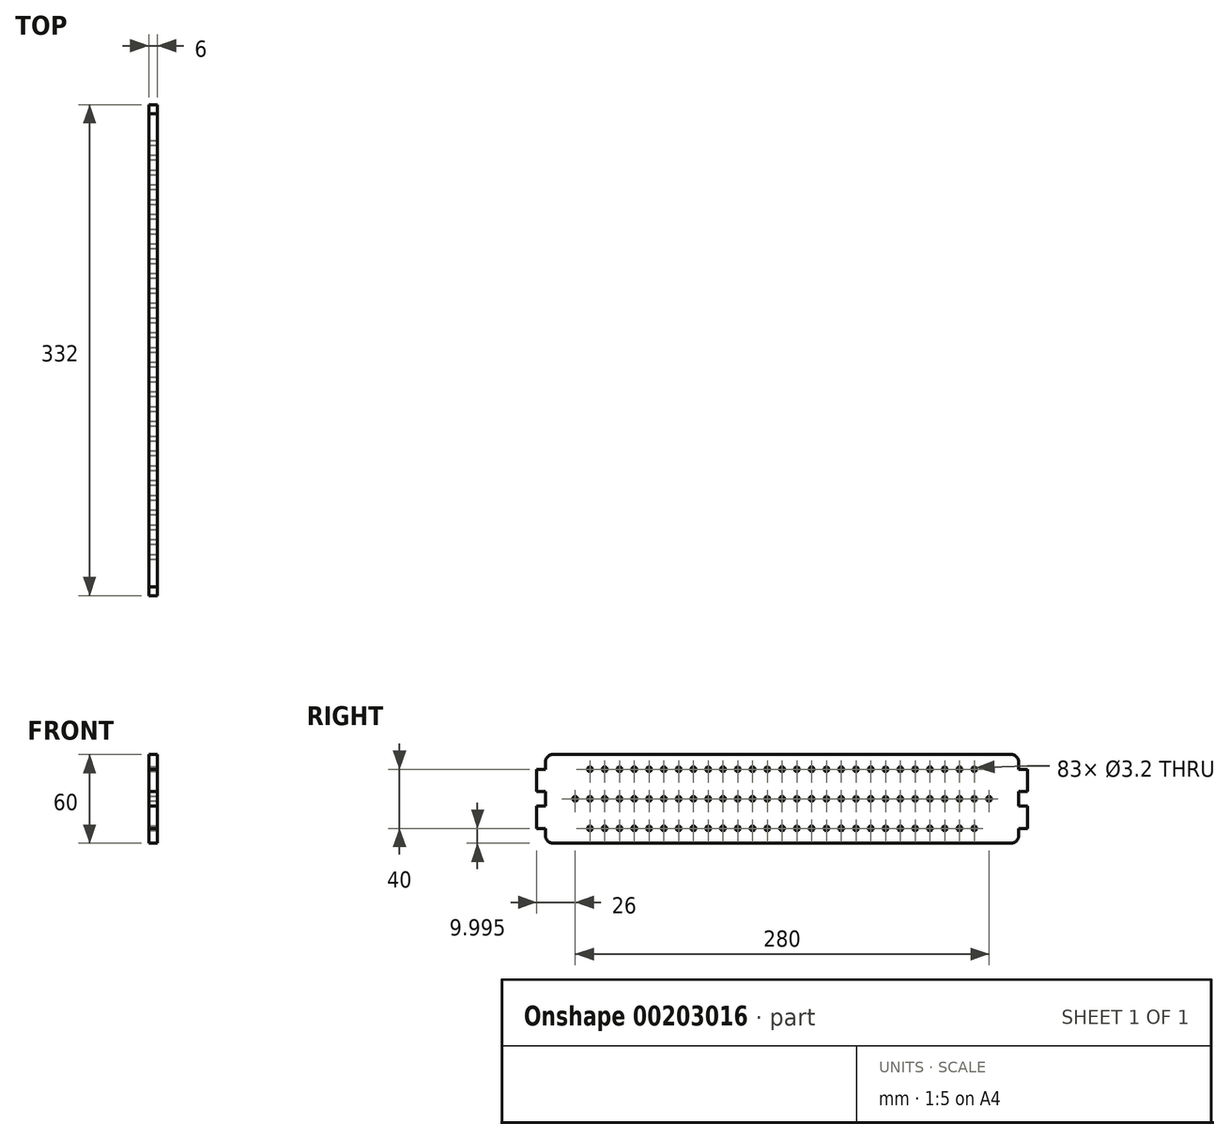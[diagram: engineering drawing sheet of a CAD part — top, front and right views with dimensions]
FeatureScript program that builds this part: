
annotation { "Feature Type Name" : "Feature", "Feature Type Description" : "" }
export const myFeature = defineFeature(function(context is Context, id is Id, definition is map)
    precondition{}
    {
        {
            var Q0;
            Q0=qCreatedBy(makeId("Right.planeOp"),FACE);
            var sketch = newSketch(context, id + "F0", { "sketchPlane" : qUnion([Q0])});
            skLineSegment(sketch, "E0", {"start": v(155, 0.59) * mm, "end": v(0, 0.59) * mm});
            skLineSegment(sketch, "E1", {"start": v(0, 0.59) * mm, "end": v(-155, 0.59) * mm});
            skArc(sketch, "E2", {"start": v(-155, 0.59) * mm, "mid": v(-158.54, 2.05) * mm, "end": v(-160, 5.59) * mm});
            skLineSegment(sketch, "E3", {"start": v(-160, 5.59) * mm, "end": v(-160, 10.59) * mm});
            skLineSegment(sketch, "E4", {"start": v(-160, 10.59) * mm, "end": v(-166, 10.59) * mm});
            skLineSegment(sketch, "E5", {"start": v(-166, 10.59) * mm, "end": v(-166, 25.59) * mm});
            skLineSegment(sketch, "E6", {"start": v(-166, 25.59) * mm, "end": v(-160, 25.59) * mm});
            skLineSegment(sketch, "E7", {"start": v(-160, 25.59) * mm, "end": v(-160, 35.59) * mm});
            skLineSegment(sketch, "E8", {"start": v(-160, 35.59) * mm, "end": v(-166, 35.59) * mm});
            skLineSegment(sketch, "E9", {"start": v(-166, 35.59) * mm, "end": v(-166, 50.59) * mm});
            skLineSegment(sketch, "E10", {"start": v(-166, 50.59) * mm, "end": v(-160, 50.59) * mm});
            skLineSegment(sketch, "E11", {"start": v(-160, 50.59) * mm, "end": v(-160, 55.59) * mm});
            skArc(sketch, "E12", {"start": v(-160, 55.59) * mm, "mid": v(-158.54, 59.12) * mm, "end": v(-155, 60.59) * mm});
            skLineSegment(sketch, "E13", {"start": v(-155, 60.59) * mm, "end": v(0, 60.59) * mm});
            skLineSegment(sketch, "E14", {"start": v(0, 60.59) * mm, "end": v(155, 60.59) * mm});
            skArc(sketch, "E15", {"start": v(155, 60.59) * mm, "mid": v(158.54, 59.12) * mm, "end": v(160, 55.59) * mm});
            skLineSegment(sketch, "E16", {"start": v(160, 55.59) * mm, "end": v(160, 50.59) * mm});
            skLineSegment(sketch, "E17", {"start": v(160, 50.59) * mm, "end": v(166, 50.59) * mm});
            skLineSegment(sketch, "E18", {"start": v(166, 50.59) * mm, "end": v(166, 35.59) * mm});
            skLineSegment(sketch, "E19", {"start": v(166, 35.59) * mm, "end": v(160, 35.59) * mm});
            skLineSegment(sketch, "E20", {"start": v(160, 35.59) * mm, "end": v(160, 25.59) * mm});
            skLineSegment(sketch, "E21", {"start": v(160, 25.59) * mm, "end": v(166, 25.59) * mm});
            skLineSegment(sketch, "E22", {"start": v(166, 25.59) * mm, "end": v(166, 10.59) * mm});
            skLineSegment(sketch, "E23", {"start": v(166, 10.59) * mm, "end": v(160, 10.59) * mm});
            skLineSegment(sketch, "E24", {"start": v(160, 10.59) * mm, "end": v(160, 5.59) * mm});
            skArc(sketch, "E25", {"start": v(160, 5.59) * mm, "mid": v(158.54, 2.05) * mm, "end": v(155, 0.59) * mm});
            skCircle(sketch, "E26", {"center": v(-130, 10.59) * mm, "radius": 1.6 * mm});
            skCircle(sketch, "E27", {"center": v(-120, 10.59) * mm, "radius": 1.6 * mm});
            skCircle(sketch, "E28", {"center": v(-110, 10.59) * mm, "radius": 1.6 * mm});
            skCircle(sketch, "E29", {"center": v(-100, 10.59) * mm, "radius": 1.6 * mm});
            skCircle(sketch, "E30", {"center": v(-90, 10.59) * mm, "radius": 1.6 * mm});
            skCircle(sketch, "E31", {"center": v(-80, 10.59) * mm, "radius": 1.6 * mm});
            skCircle(sketch, "E32", {"center": v(-70, 10.59) * mm, "radius": 1.6 * mm});
            skCircle(sketch, "E33", {"center": v(-60, 10.59) * mm, "radius": 1.6 * mm});
            skCircle(sketch, "E34", {"center": v(-50, 10.59) * mm, "radius": 1.6 * mm});
            skCircle(sketch, "E35", {"center": v(-40, 10.59) * mm, "radius": 1.6 * mm});
            skCircle(sketch, "E36", {"center": v(-30, 10.59) * mm, "radius": 1.6 * mm});
            skCircle(sketch, "E37", {"center": v(-20, 10.59) * mm, "radius": 1.6 * mm});
            skCircle(sketch, "E38", {"center": v(-10, 10.59) * mm, "radius": 1.6 * mm});
            skCircle(sketch, "E39", {"center": v(0, 10.59) * mm, "radius": 1.6 * mm});
            skCircle(sketch, "E40", {"center": v(10, 10.59) * mm, "radius": 1.6 * mm});
            skCircle(sketch, "E41", {"center": v(20, 10.59) * mm, "radius": 1.6 * mm});
            skCircle(sketch, "E42", {"center": v(30, 10.59) * mm, "radius": 1.6 * mm});
            skCircle(sketch, "E43", {"center": v(40, 10.59) * mm, "radius": 1.6 * mm});
            skCircle(sketch, "E44", {"center": v(50, 10.59) * mm, "radius": 1.6 * mm});
            skCircle(sketch, "E45", {"center": v(60, 10.59) * mm, "radius": 1.6 * mm});
            skCircle(sketch, "E46", {"center": v(70, 10.59) * mm, "radius": 1.6 * mm});
            skCircle(sketch, "E47", {"center": v(80, 10.59) * mm, "radius": 1.6 * mm});
            skCircle(sketch, "E48", {"center": v(90, 10.59) * mm, "radius": 1.6 * mm});
            skCircle(sketch, "E49", {"center": v(100, 10.59) * mm, "radius": 1.6 * mm});
            skCircle(sketch, "E50", {"center": v(110, 10.59) * mm, "radius": 1.6 * mm});
            skCircle(sketch, "E51", {"center": v(120, 10.59) * mm, "radius": 1.6 * mm});
            skCircle(sketch, "E52", {"center": v(130, 10.59) * mm, "radius": 1.6 * mm});
            skCircle(sketch, "E53", {"center": v(-140, 30.59) * mm, "radius": 1.6 * mm});
            skCircle(sketch, "E54", {"center": v(-130, 30.59) * mm, "radius": 1.6 * mm});
            skCircle(sketch, "E55", {"center": v(-120, 30.59) * mm, "radius": 1.6 * mm});
            skCircle(sketch, "E56", {"center": v(-110, 30.59) * mm, "radius": 1.6 * mm});
            skCircle(sketch, "E57", {"center": v(-100, 30.59) * mm, "radius": 1.6 * mm});
            skCircle(sketch, "E58", {"center": v(-90, 30.59) * mm, "radius": 1.6 * mm});
            skCircle(sketch, "E59", {"center": v(-80, 30.59) * mm, "radius": 1.6 * mm});
            skCircle(sketch, "E60", {"center": v(-70, 30.59) * mm, "radius": 1.6 * mm});
            skCircle(sketch, "E61", {"center": v(-60, 30.59) * mm, "radius": 1.6 * mm});
            skCircle(sketch, "E62", {"center": v(-50, 30.59) * mm, "radius": 1.6 * mm});
            skCircle(sketch, "E63", {"center": v(-40, 30.59) * mm, "radius": 1.6 * mm});
            skCircle(sketch, "E64", {"center": v(-30, 30.59) * mm, "radius": 1.6 * mm});
            skCircle(sketch, "E65", {"center": v(-20, 30.59) * mm, "radius": 1.6 * mm});
            skCircle(sketch, "E66", {"center": v(-10, 30.59) * mm, "radius": 1.6 * mm});
            skCircle(sketch, "E67", {"center": v(0, 30.59) * mm, "radius": 1.6 * mm});
            skCircle(sketch, "E68", {"center": v(10, 30.59) * mm, "radius": 1.6 * mm});
            skCircle(sketch, "E69", {"center": v(20, 30.59) * mm, "radius": 1.6 * mm});
            skCircle(sketch, "E70", {"center": v(30, 30.59) * mm, "radius": 1.6 * mm});
            skCircle(sketch, "E71", {"center": v(40, 30.59) * mm, "radius": 1.6 * mm});
            skCircle(sketch, "E72", {"center": v(50, 30.59) * mm, "radius": 1.6 * mm});
            skCircle(sketch, "E73", {"center": v(60, 30.59) * mm, "radius": 1.6 * mm});
            skCircle(sketch, "E74", {"center": v(70, 30.59) * mm, "radius": 1.6 * mm});
            skCircle(sketch, "E75", {"center": v(80, 30.59) * mm, "radius": 1.6 * mm});
            skCircle(sketch, "E76", {"center": v(90, 30.59) * mm, "radius": 1.6 * mm});
            skCircle(sketch, "E77", {"center": v(100, 30.59) * mm, "radius": 1.6 * mm});
            skCircle(sketch, "E78", {"center": v(110, 30.59) * mm, "radius": 1.6 * mm});
            skCircle(sketch, "E79", {"center": v(120, 30.59) * mm, "radius": 1.6 * mm});
            skCircle(sketch, "E80", {"center": v(130, 30.59) * mm, "radius": 1.6 * mm});
            skCircle(sketch, "E81", {"center": v(140, 30.59) * mm, "radius": 1.6 * mm});
            skCircle(sketch, "E82", {"center": v(-130, 50.59) * mm, "radius": 1.6 * mm});
            skCircle(sketch, "E83", {"center": v(-120, 50.59) * mm, "radius": 1.6 * mm});
            skCircle(sketch, "E84", {"center": v(-110, 50.59) * mm, "radius": 1.6 * mm});
            skCircle(sketch, "E85", {"center": v(-100, 50.59) * mm, "radius": 1.6 * mm});
            skCircle(sketch, "E86", {"center": v(-90, 50.59) * mm, "radius": 1.6 * mm});
            skCircle(sketch, "E87", {"center": v(-80, 50.59) * mm, "radius": 1.6 * mm});
            skCircle(sketch, "E88", {"center": v(-70, 50.59) * mm, "radius": 1.6 * mm});
            skCircle(sketch, "E89", {"center": v(-60, 50.59) * mm, "radius": 1.6 * mm});
            skCircle(sketch, "E90", {"center": v(-50, 50.59) * mm, "radius": 1.6 * mm});
            skCircle(sketch, "E91", {"center": v(-40, 50.59) * mm, "radius": 1.6 * mm});
            skCircle(sketch, "E92", {"center": v(-30, 50.59) * mm, "radius": 1.6 * mm});
            skCircle(sketch, "E93", {"center": v(-20, 50.59) * mm, "radius": 1.6 * mm});
            skCircle(sketch, "E94", {"center": v(-10, 50.59) * mm, "radius": 1.6 * mm});
            skCircle(sketch, "E95", {"center": v(0, 50.59) * mm, "radius": 1.6 * mm});
            skCircle(sketch, "E96", {"center": v(10, 50.59) * mm, "radius": 1.6 * mm});
            skCircle(sketch, "E97", {"center": v(20, 50.59) * mm, "radius": 1.6 * mm});
            skCircle(sketch, "E98", {"center": v(30, 50.59) * mm, "radius": 1.6 * mm});
            skCircle(sketch, "E99", {"center": v(40, 50.59) * mm, "radius": 1.6 * mm});
            skCircle(sketch, "E100", {"center": v(50, 50.59) * mm, "radius": 1.6 * mm});
            skCircle(sketch, "E101", {"center": v(60, 50.59) * mm, "radius": 1.6 * mm});
            skCircle(sketch, "E102", {"center": v(70, 50.59) * mm, "radius": 1.6 * mm});
            skCircle(sketch, "E103", {"center": v(80, 50.59) * mm, "radius": 1.6 * mm});
            skCircle(sketch, "E104", {"center": v(90, 50.59) * mm, "radius": 1.6 * mm});
            skCircle(sketch, "E105", {"center": v(100, 50.59) * mm, "radius": 1.6 * mm});
            skCircle(sketch, "E106", {"center": v(110, 50.59) * mm, "radius": 1.6 * mm});
            skCircle(sketch, "E107", {"center": v(120, 50.59) * mm, "radius": 1.6 * mm});
            skCircle(sketch, "E108", {"center": v(130, 50.59) * mm, "radius": 1.6 * mm});
            skSolve(sketch);
        }
        {
            var Q0;
            Q0 = qSketchRegion(id + "F0", true);
            extrude(context, id + "F1", {"entities" : qUnion([Q0]), "depth" : 6 * mm});
        }
    });
